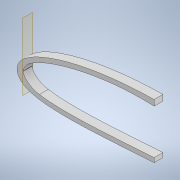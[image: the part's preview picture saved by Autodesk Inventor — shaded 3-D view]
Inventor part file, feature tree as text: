
AUTODESK INVENTOR PART (.ipt)
format: ipt  version: 2022.3 (Build 263350000, 350)  size: 482,304 bytes
history: native  units: mm
features: sketch x6, extrude x5, thicken_offset x3, projected_geometry x2, shell x1, plane x1, other x1
ambient origin geometry x8: Origin, YZ Plane, XZ Plane, XY Plane, X Axis, Y Axis, Z Axis, Center Point
bodies: Solid1 (feature_tree)
feature tree (19):
  extrude  "Extrusion1"  Depth=10.0mm
  shell  "Shell1"  Thickness=1.0mm
  thicken_offset  "Thicken1"
  extrude  "Extrusion27"  TaperAngle=0.0deg  [1 undecoded]
  thicken_offset  "Thicken3"
  extrude  "Extrusion29"  Depth=20.0mm
  plane  "Work Plane5"
  other  "Bend Part2"
  thicken_offset  "Thicken5"
  extrude  "Extrusion30"  Depth=10.0mm TaperAngle=0.0deg
  extrude  "Extrusion31"  Depth=10.0mm
  sketch  "Sketch3"  dims[d0=10.0mm d1=0.0mm d2=3.0mm d159=1.0mm d160=2.0mm]
  sketch  "Sketch48"  dims[d236=190.0mm d237=0.0mm d238=0.0mm]
  sketch  "Sketch55"  dims[d249=2.0mm d250=1.0mm d254=20.0mm]
  projected_geometry  "Projected Loop32"
  sketch  "Sketch57"  dims[d255=8.0mm d256=10.0mm d257=0.0mm]
  sketch  "Sketch58"  dims[d262=10.0mm d263=0.349066mm d264=1.0mm]
  projected_geometry  "Projected Loop34"
  sketch  "Sketch59"  dims[d265=1.0mm d268=100.0mm d269=5.0mm d270=10.0mm d271=0.0mm d272=150.0mm d273=100.0mm d274=0.0mm]
note: 1 required parameter value undecoded (feature->parameter linkage not recoverable at this tier; creation-order binding heuristic only, values carry confidence <= 0.55)
